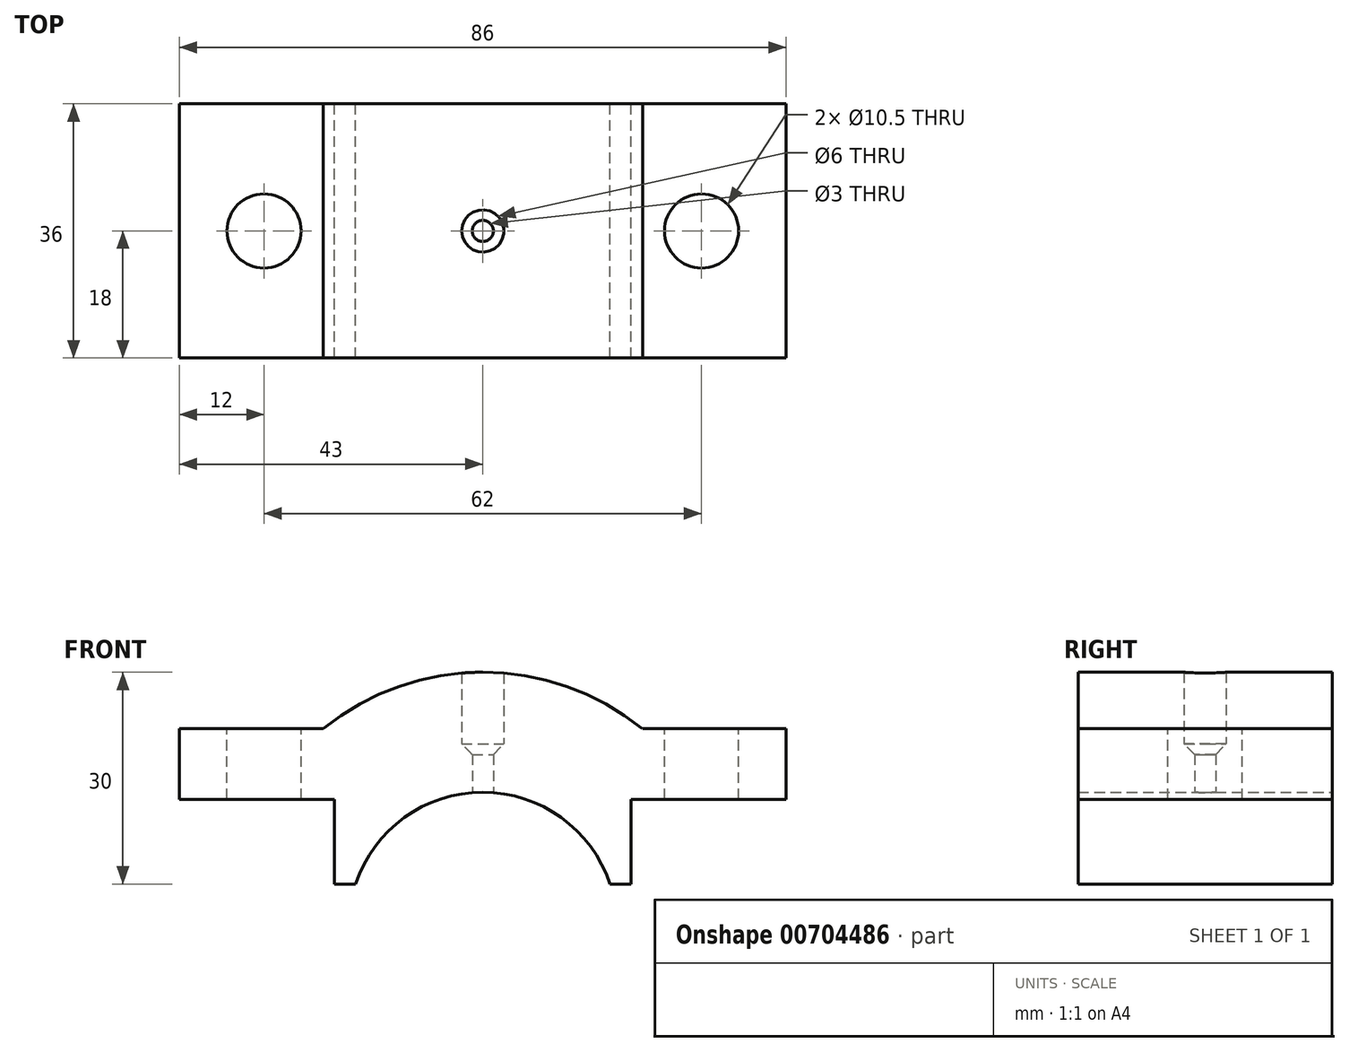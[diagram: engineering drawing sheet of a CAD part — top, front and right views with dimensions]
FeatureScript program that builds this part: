
annotation { "Feature Type Name" : "Feature", "Feature Type Description" : "" }
export const myFeature = defineFeature(function(context is Context, id is Id, definition is map)
    precondition{}
    {
        {
            var Q0;
            Q0=qCreatedBy(makeId("Front.planeOp"),FACE);
            var sketch = newSketch(context, id + "F0", { "sketchPlane" : qUnion([Q0])});
            skArc(sketch, "E0", {"start": v(18.03, 6) * mm, "mid": v(0, 19) * mm, "end": v(-18.03, 6) * mm});
            skLineSegment(sketch, "E1", {"start": v(0, 0) * mm, "end": v(0, 6) * mm});
            skLineSegment(sketch, "E2", {"start": v(-18.03, 6) * mm, "end": v(-21.03, 6) * mm});
            skLineSegment(sketch, "E3", {"start": v(18.03, 6) * mm, "end": v(21.03, 6) * mm});
            skLineSegment(sketch, "E4", {"start": v(21.03, 6) * mm, "end": v(21.03, 18) * mm});
            skLineSegment(sketch, "E5", {"start": v(21.03, 18) * mm, "end": v(43, 18) * mm});
            skLineSegment(sketch, "E6", {"start": v(43, 18) * mm, "end": v(43, 28) * mm});
            skLineSegment(sketch, "E7", {"start": v(43, 28) * mm, "end": v(22.63, 28) * mm});
            skLineSegment(sketch, "E8", {"start": v(-43, 28) * mm, "end": v(-43, 18) * mm});
            skLineSegment(sketch, "E9", {"start": v(-43, 18) * mm, "end": v(-21.03, 18) * mm});
            skLineSegment(sketch, "E10", {"start": v(-21.03, 18) * mm, "end": v(-21.03, 6) * mm});
            skArc(sketch, "E11", {"start": v(22.63, 28) * mm, "mid": v(0, 36) * mm, "end": v(-22.63, 28) * mm});
            skLineSegment(sketch, "E12.trimOffspring", {"start": v(-22.63, 28) * mm, "end": v(-43, 28) * mm});
            skSolve(sketch);
        }
        {
            var Q0;
            Q0=qSketchRegion(id+"F0",true);
            extrude(context, id + "F1", {"entities" : qUnion([Q0]), "endBound" : BoundingType.SYMMETRIC, "depth" : 36 * mm, "offsetDistance" : 25 * mm});
        }
        {
            var Q0;
            Q0=makeQuery(id+"F1.opExtrude","SWEPT_FACE",FACE,{"disambiguationData":[OSD([sQuery(id+"F0.wireOp",EDGE,"E7")])]});
            var sketch = newSketch(context, id + "F2", { "sketchPlane" : qUnion([Q0])});
            skCircle(sketch, "E13", {"center": v(-31, 0) * mm, "radius": 5.25 * mm});
            skPoint(sketch, "E13.centerSnap0", {"position": v(43, 0) * mm});
            skCircle(sketch, "E14", {"center": v(31, 0) * mm, "radius": 5.25 * mm});
            skSolve(sketch);
        }
        {
            var Q0;
            Q0=qSketchRegion(id+"F2",true);
            extrude(context, id + "F3", {"entities" : qUnion([Q0]), "operationType" : NewBodyOperationType.REMOVE, "oppositeDirection" : true, "depth" : 25 * mm, "offsetDistance" : 25 * mm});
        }
        {
            var Q0;
            Q0=qCreatedBy(makeId("Front.planeOp"),FACE);
            var sketch = newSketch(context, id + "F4", { "sketchPlane" : qUnion([Q0])});
            skLineSegment(sketch, "E15", {"start": v(0, 50.86) * mm, "end": v(0, 0) * mm, "construction": true});
            skLineSegment(sketch, "E16", {"start": v(0, 40.12) * mm, "end": v(3, 40.07) * mm});
            skLineSegment(sketch, "E17", {"start": v(3, 40.07) * mm, "end": v(3, 25.86) * mm});
            skLineSegment(sketch, "E18", {"start": v(0, 17.16) * mm, "end": v(0, 40.12) * mm});
            skLineSegment(sketch, "E19", {"start": v(1.5, 24.36) * mm, "end": v(1.5, 17.16) * mm});
            skLineSegment(sketch, "E20", {"start": v(1.5, 17.16) * mm, "end": v(0, 17.16) * mm});
            skLineSegment(sketch, "E21", {"start": v(1.5, 24.36) * mm, "end": v(3, 25.86) * mm});
            skSolve(sketch);
        }
        {
            var Q0;
            Q0=qSketchRegion(id+"F4",true);
            var Q1;
            Q1=sQuery(id+"F4.wireOp",EDGE,"E15");
            revolve(context, id + "F5", {"operationType" : NewBodyOperationType.REMOVE, "entities" : qUnion([Q0]), "axis" : qUnion([Q1]), "revolveType" : RevolveType.FULL, "oppositeDirection" : true});
        }
    });
